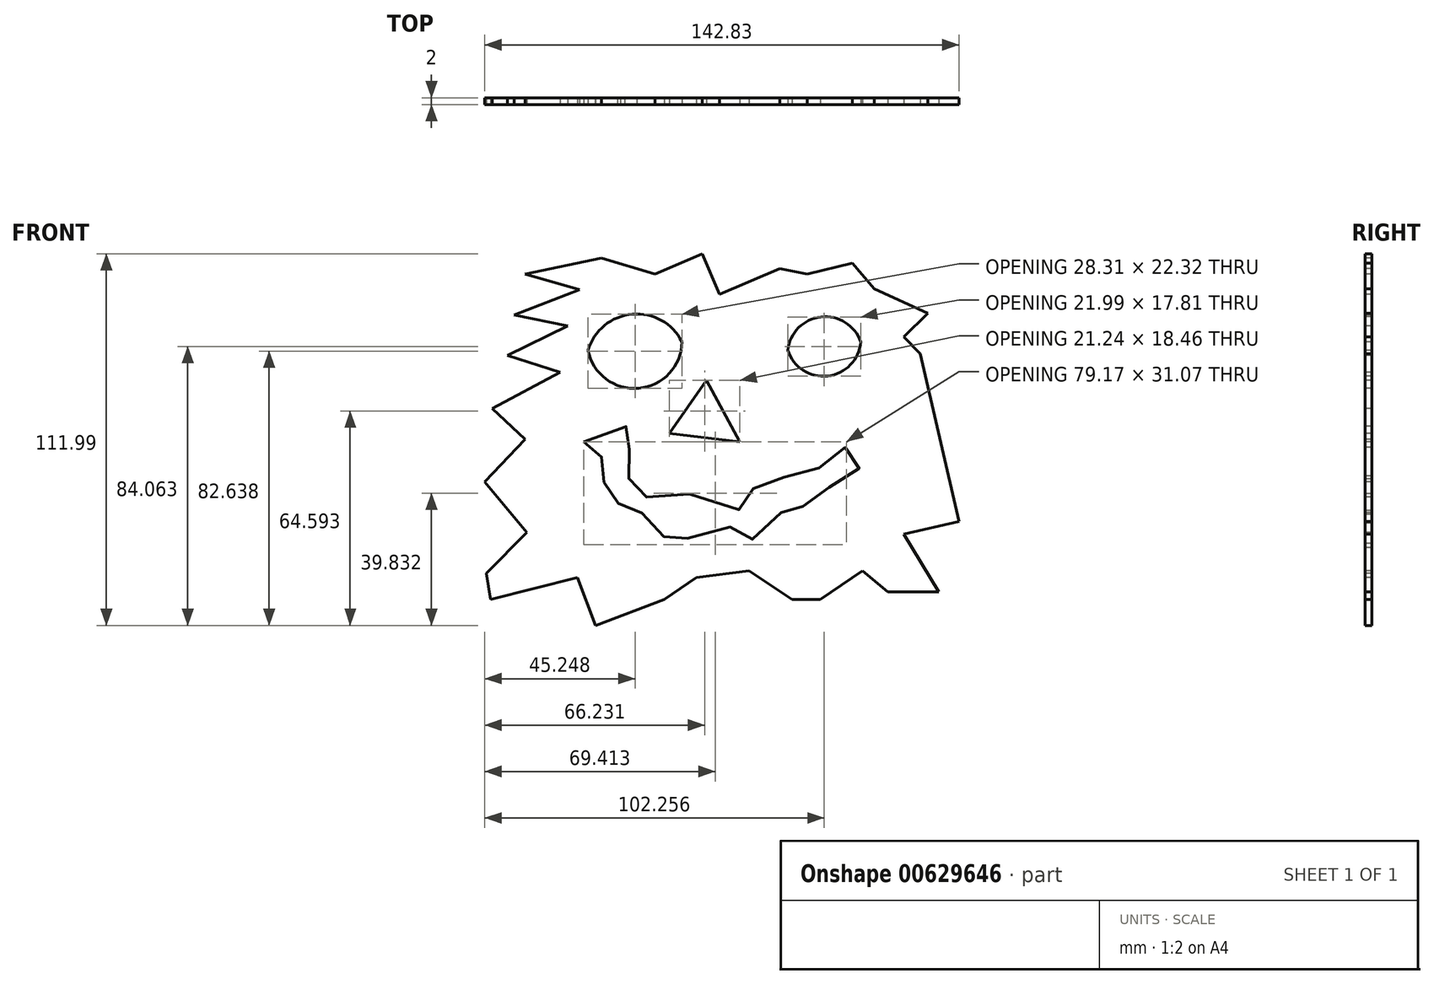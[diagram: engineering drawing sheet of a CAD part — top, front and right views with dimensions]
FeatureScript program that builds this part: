
annotation { "Feature Type Name" : "Feature", "Feature Type Description" : "" }
export const myFeature = defineFeature(function(context is Context, id is Id, definition is map)
    precondition{}
    {
        {
            var Q0;
            Q0=qCreatedBy(makeId("Front.planeOp"),FACE);
            var sketch = newSketch(context, id + "F0", { "sketchPlane" : qUnion([Q0])});
            skLineSegment(sketch, "E0", {"start": v(-71.04, -47.28) * mm, "end": v(-58.9, -34.89) * mm});
            skLineSegment(sketch, "E1", {"start": v(-58.9, -34.89) * mm, "end": v(-71.54, -19.72) * mm});
            skLineSegment(sketch, "E2", {"start": v(-71.54, -19.72) * mm, "end": v(-59.41, -6.83) * mm});
            skLineSegment(sketch, "E3", {"start": v(-59.41, -6.83) * mm, "end": v(-69.3, 2.47) * mm});
            skLineSegment(sketch, "E4", {"start": v(-69.3, 2.47) * mm, "end": v(-48.8, 13.4) * mm});
            skLineSegment(sketch, "E5", {"start": v(-48.8, 13.4) * mm, "end": v(-64.72, 18.46) * mm});
            skLineSegment(sketch, "E6", {"start": v(-64.72, 18.46) * mm, "end": v(-46.52, 27.3) * mm});
            skLineSegment(sketch, "E7", {"start": v(-46.52, 27.3) * mm, "end": v(-62.7, 30.59) * mm});
            skLineSegment(sketch, "E8", {"start": v(-62.7, 30.59) * mm, "end": v(-42.98, 38.17) * mm});
            skLineSegment(sketch, "E9", {"start": v(-42.98, 38.17) * mm, "end": v(-59.41, 42.98) * mm});
            skLineSegment(sketch, "E10", {"start": v(-59.41, 42.98) * mm, "end": v(-36.4, 47.78) * mm});
            skLineSegment(sketch, "E11", {"start": v(-36.4, 47.78) * mm, "end": v(-20.22, 42.98) * mm});
            skLineSegment(sketch, "E12", {"start": v(-20.22, 42.98) * mm, "end": v(-6.07, 49.04) * mm});
            skLineSegment(sketch, "E13", {"start": v(-6.07, 49.04) * mm, "end": v(-0.82, 36.8) * mm});
            skLineSegment(sketch, "E14", {"start": v(-0.82, 36.8) * mm, "end": v(17.33, 44.6) * mm});
            skLineSegment(sketch, "E15", {"start": v(17.33, 44.6) * mm, "end": v(25.53, 42.98) * mm});
            skLineSegment(sketch, "E16", {"start": v(25.53, 42.98) * mm, "end": v(39.19, 46.26) * mm});
            skLineSegment(sketch, "E17", {"start": v(39.19, 46.26) * mm, "end": v(45.76, 38.43) * mm});
            skLineSegment(sketch, "E18", {"start": v(45.76, 38.43) * mm, "end": v(61.94, 31.1) * mm});
            skLineSegment(sketch, "E19", {"start": v(61.94, 31.1) * mm, "end": v(54.6, 24.02) * mm});
            skLineSegment(sketch, "E20", {"start": v(54.6, 24.02) * mm, "end": v(59.57, 18.88) * mm});
            skLineSegment(sketch, "E21", {"start": v(59.57, 18.88) * mm, "end": v(71.3, -31.6) * mm});
            skLineSegment(sketch, "E22", {"start": v(71.3, -31.6) * mm, "end": v(54.6, -35.48) * mm});
            skLineSegment(sketch, "E23", {"start": v(54.6, -35.48) * mm, "end": v(65.22, -52.84) * mm});
            skLineSegment(sketch, "E24", {"start": v(65.22, -52.84) * mm, "end": v(49.8, -52.84) * mm});
            skLineSegment(sketch, "E25", {"start": v(49.8, -52.84) * mm, "end": v(42.22, -46.52) * mm});
            skLineSegment(sketch, "E26", {"start": v(42.22, -46.52) * mm, "end": v(29.58, -55.11) * mm});
            skLineSegment(sketch, "E27", {"start": v(29.58, -55.11) * mm, "end": v(20.98, -55.11) * mm});
            skLineSegment(sketch, "E28", {"start": v(20.98, -55.11) * mm, "end": v(8.09, -46.52) * mm});
            skLineSegment(sketch, "E29", {"start": v(8.09, -46.52) * mm, "end": v(-7.84, -48.54) * mm});
            skLineSegment(sketch, "E30", {"start": v(-7.84, -48.54) * mm, "end": v(-17.44, -55.11) * mm});
            skLineSegment(sketch, "E31", {"start": v(-17.44, -55.11) * mm, "end": v(-38.17, -62.95) * mm});
            skLineSegment(sketch, "E32", {"start": v(-38.17, -62.95) * mm, "end": v(-43.62, -48.54) * mm});
            skLineSegment(sketch, "E33", {"start": v(-43.62, -48.54) * mm, "end": v(-69.78, -55.11) * mm});
            skLineSegment(sketch, "E34", {"start": v(-69.78, -55.11) * mm, "end": v(-71.04, -47.28) * mm});
            skArc(sketch, "E35", {"start": v(-40.45, 19.97) * mm, "mid": v(-25.16, 8.53) * mm, "end": v(-12.13, 22.5) * mm});
            skArc(sketch, "E36", {"start": v(-12.13, 22.5) * mm, "mid": v(-27.15, 30.85) * mm, "end": v(-40.45, 19.97) * mm});
            skArc(sketch, "E37", {"start": v(41.71, 22.5) * mm, "mid": v(29.7, 30.02) * mm, "end": v(19.72, 19.97) * mm});
            skArc(sketch, "E38", {"start": v(19.72, 19.97) * mm, "mid": v(31.75, 12.2) * mm, "end": v(41.71, 22.5) * mm});
            skFitSpline(sketch, "E39", {"points": [v(-41.71, -7.58) * mm, v(-36.4, -10.37) * mm, v(-38.17, -17.95) * mm, v(-30.84, -22.5) * mm, v(-31.35, -28.57) * mm, v(-18.96, -30.34) * mm, v(-16.69, -39.44) * mm, v(0, -32.1) * mm, v(7.08, -38.17) * mm, v(16.18, -29.33) * mm, v(22.25, -29.33) * mm, v(27.3, -23) * mm, v(37.92, -19.47) * mm, v(41.46, -11.12) * mm, v(32.61, -10.62) * mm, v(26.04, -18.46) * mm, v(10.62, -18.7) * mm, v(8.09, -27.8) * mm, v(-9.1, -23.51) * mm, v(-24.27, -24.02) * mm, v(-28.06, -18.96) * mm, v(-29.07, -12.13) * mm, v(-26.3, -3.29) * mm, v(-41.71, -7.58) * mm]});
            skLineSegment(sketch, "E40", {"start": v(-4.8, 10.87) * mm, "end": v(-15.93, -5.06) * mm});
            skLineSegment(sketch, "E41", {"start": v(-15.93, -5.06) * mm, "end": v(5.3, -7.58) * mm});
            skLineSegment(sketch, "E42", {"start": v(5.3, -7.58) * mm, "end": v(-4.8, 10.87) * mm});
            skCircle(sketch, "E43", {"center": v(-9.86, -2.78) * mm, "radius": 2.08 * mm});
            skCircle(sketch, "E44", {"center": v(0, -2.78) * mm, "radius": 1.79 * mm});
            skSolve(sketch);
        }
        {
            var Q0;
            Q0=makeQuery(id+"F0.imprint","IMPRINT",FACE,{"disambiguationData":[TD([[makeQuery(id+"F0.imprint","IMPRINT",EDGE,{"derivedFrom":sQuery(id+"F0.wireOp",EDGE,"E0")}),-1.0]])]});
            extrude(context, id + "F1", {"entities" : qUnion([Q0]), "oppositeDirection" : true, "depth" : 2 * mm, "offsetDistance" : 25 * mm});
        }
    });
